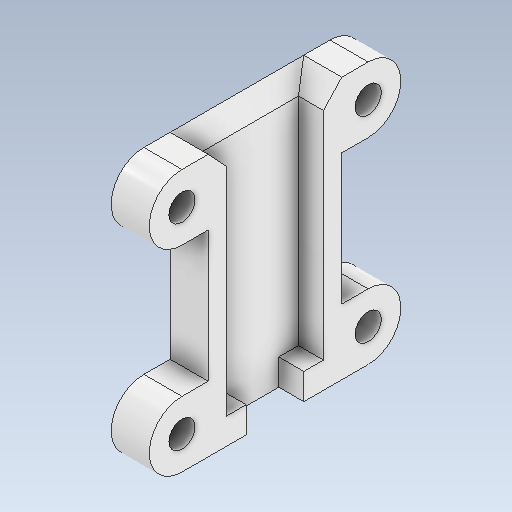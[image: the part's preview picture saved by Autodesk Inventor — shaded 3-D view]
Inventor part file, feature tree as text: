
AUTODESK INVENTOR PART (.ipt)
format: ipt  version: 2020 (Build 240168000, 168)  size: 239,104 bytes
history: native  units: in
note: dims shown in document units (in); Inventor stores cm internally (conversion verified against a paired STEP export)
features: extrude x6, sketch x6, projected_geometry x5, chamfer x3
ambient origin geometry x8: Origin, YZ Plane, XZ Plane, XY Plane, X Axis, Y Axis, Z Axis, Center Point
bodies: Solid1 (feature_tree)
feature tree (20):
  extrude  "Extrusion1"  Depth=0.7874in
  extrude  "Extrusion2"  Depth=0.0551in
  extrude  "Extrusion3"  Depth=0.0752in
  chamfer  "Chamfer1"  Distance=0.1146in
  chamfer  "Chamfer2"  Distance=0.0787in
  chamfer  "Chamfer3"  Distance=0.1969in
  extrude  "Extrusion4"  Depth=0.1146in TaperAngle=0.0deg
  extrude  "Extrusion5"  Depth=0.0394in
  extrude  "Extrusion6"  Depth=0.0551in
  sketch  "Sketch1"  dims[d0=0.402in d1=0.7874in]
  sketch  "Sketch2"  dims[d2=0.1146in d3=0.0in d4=0.0551in]
  projected_geometry  "Projected Loop1"
  sketch  "Sketch3"  dims[d5=0.0394in d6=0.0752in]
  projected_geometry  "Projected Loop2"
  sketch  "Sketch4"  dims[d7=0.2913in d8=0.1146in d9=0.0in]
  projected_geometry  "Projected Loop3"
  sketch  "Sketch5"  dims[d10=0.1969in]
  projected_geometry  "Projected Loop4"
  sketch  "Sketch6"  dims[d11=0.0787in d12=0.0787in d13=0.1969in d14=0.1146in d15=0.0in d16=0.0394in d17=0.0787in d18=0.8496in d19=0.0551in d20=0.0787in d21=0.9138in d22=0.0551in d23=0.0787in d24=0.9138in d25=0.0197in d26=0.0787in d27=0.0in d28=0.3937in d29=0.0in d30=0.0394in d31=0.0394in d32=0.0752in d33=0.3937in d34=0.0in]
  projected_geometry  "Projected Loop5"
